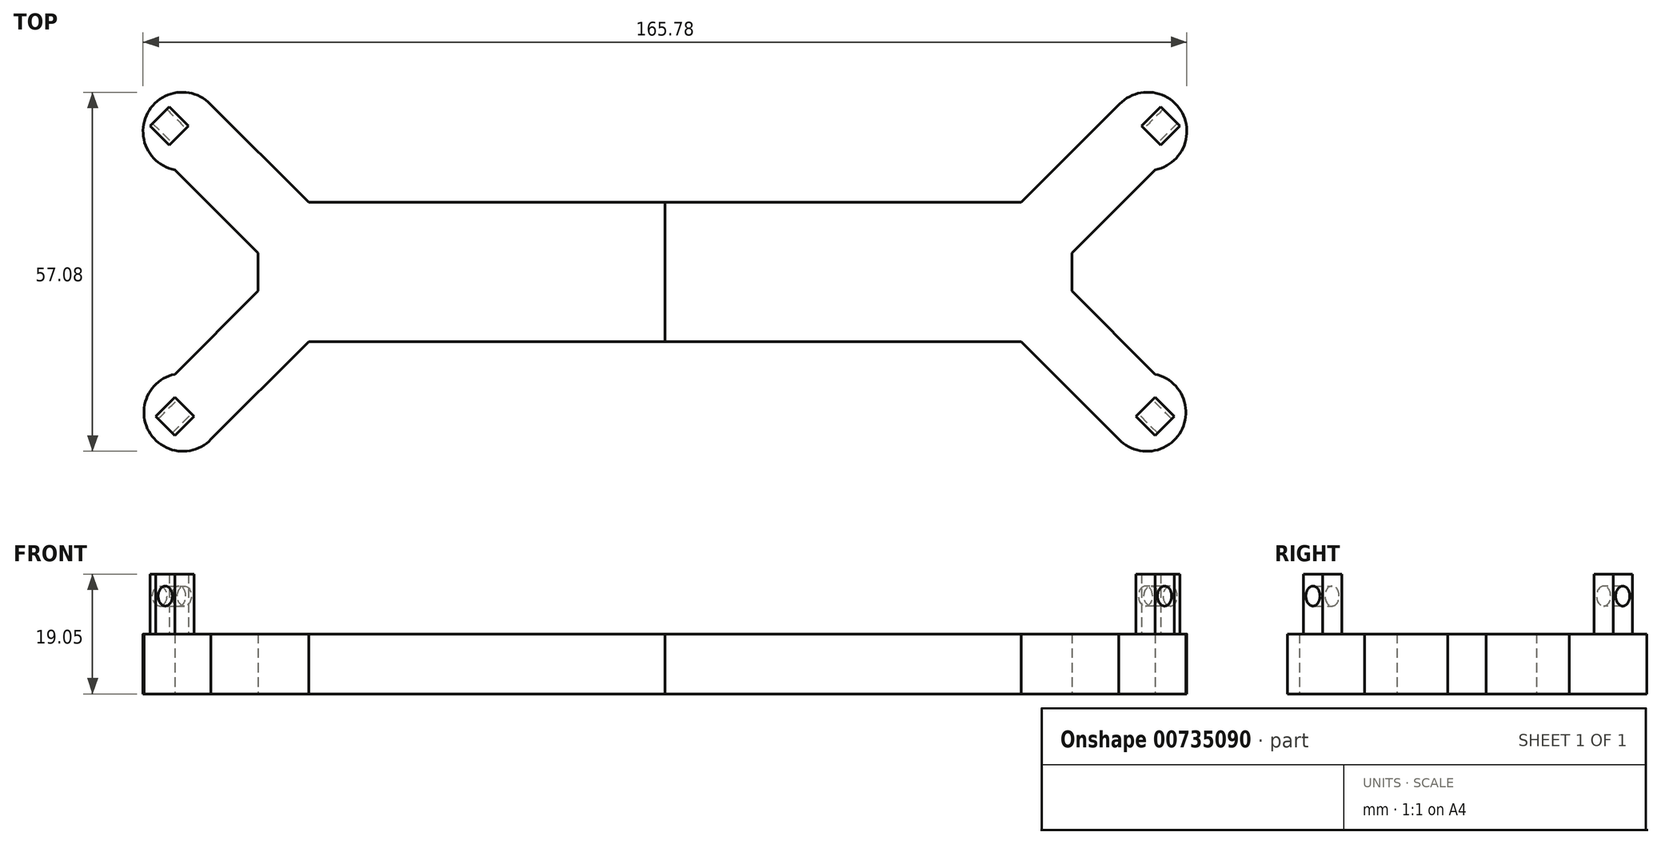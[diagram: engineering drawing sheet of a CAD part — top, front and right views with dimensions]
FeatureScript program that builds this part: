
annotation { "Feature Type Name" : "Feature", "Feature Type Description" : "" }
export const myFeature = defineFeature(function(context is Context, id is Id, definition is map)
    precondition{}
    {
        {
            var Q0;
            Q0=qCreatedBy(makeId("Top.planeOp"),FACE);
            var sketch = newSketch(context, id + "F0", { "sketchPlane" : qUnion([Q0])});
            skLineSegment(sketch, "E0.bottom", {"start": v(0, -10.57) * mm, "end": v(-64.63, -10.57) * mm});
            skLineSegment(sketch, "E0.top", {"start": v(0, 11.58) * mm, "end": v(-64.63, 11.58) * mm});
            skLineSegment(sketch, "E0.left", {"start": v(0, -10.57) * mm, "end": v(0, 11.58) * mm});
            skLineSegment(sketch, "E0.right", {"start": v(-64.63, -10.57) * mm, "end": v(-64.63, 11.58) * mm});
            skLineSegment(sketch, "E1", {"start": v(-56.58, 11.58) * mm, "end": v(-72.3, 27.31) * mm});
            skLineSegment(sketch, "E2", {"start": v(-64.63, 3.53) * mm, "end": v(-77.85, 16.75) * mm});
            skLineSegment(sketch, "E3", {"start": v(-56.58, -10.57) * mm, "end": v(-72.1, -26.09) * mm});
            skLineSegment(sketch, "E4", {"start": v(-64.63, -2.52) * mm, "end": v(-77.85, -15.74) * mm});
            skCircle(sketch, "E5", {"center": v(-76.67, 22.87) * mm, "radius": 6.23 * mm});
            skPoint(sketch, "E5.third.point", {"position": v(-81.03, 27.31) * mm});
            skCircle(sketch, "E6", {"center": v(-76.56, -21.8) * mm, "radius": 6.2 * mm});
            skPoint(sketch, "E6.third.point", {"position": v(-81.03, -26.09) * mm});
            skSolve(sketch);
        }
        {
            var Q0;
            Q0 = qSketchRegion(id + "F0", true);
            extrude(context, id + "F1", {"entities" : qUnion([Q0]), "depth" : 9.52 * mm, "offsetDistance" : 25.4 * mm});
        }
        {
            var Q0;
            Q0=makeQuery(id+"F1.opExtrude","CAP_FACE",FACE,{"disambiguationData":[OSD([sQuery(id+"F0.wireOp",EDGE,"E0.bottom"),sQuery(id+"F0.wireOp",EDGE,"E0.top"),sQuery(id+"F0.wireOp",EDGE,"E0.left"),sQuery(id+"F0.wireOp",EDGE,"E0.right"),sQuery(id+"F0.wireOp",EDGE,"E1"),sQuery(id+"F0.wireOp",EDGE,"E2"),sQuery(id+"F0.wireOp",EDGE,"E3"),sQuery(id+"F0.wireOp",EDGE,"E4"),sQuery(id+"F0.wireOp",EDGE,"E5"),sQuery(id+"F0.wireOp",EDGE,"E6")])],"isStart":false});
            var sketch = newSketch(context, id + "F2", { "sketchPlane" : qUnion([Q0])});
            skLineSegment(sketch, "E7.bottom", {"start": v(-78.74, 20.7) * mm, "end": v(-81.77, 23.74) * mm});
            skLineSegment(sketch, "E7.top", {"start": v(-75.7, 23.74) * mm, "end": v(-78.74, 26.78) * mm});
            skLineSegment(sketch, "E7.left", {"start": v(-78.74, 20.7) * mm, "end": v(-75.7, 23.74) * mm});
            skLineSegment(sketch, "E7.right", {"start": v(-81.77, 23.74) * mm, "end": v(-78.74, 26.78) * mm});
            skPoint(sketch, "E7.middle", {"position": v(-77.85, 23.22) * mm});
            skLineSegment(sketch, "E8.bottom", {"start": v(-74.81, -22.43) * mm, "end": v(-77.85, -19.4) * mm});
            skLineSegment(sketch, "E8.top", {"start": v(-77.85, -25.46) * mm, "end": v(-80.88, -22.43) * mm});
            skLineSegment(sketch, "E8.left", {"start": v(-74.81, -22.43) * mm, "end": v(-77.85, -25.46) * mm});
            skLineSegment(sketch, "E8.right", {"start": v(-77.85, -19.4) * mm, "end": v(-80.88, -22.43) * mm});
            skPoint(sketch, "E8.middle", {"position": v(-77.85, -21.54) * mm});
            skSolve(sketch);
        }
        {
            var Q0;
            Q0 = qSketchRegion(id + "F2", true);
            extrude(context, id + "F3", {"entities" : qUnion([Q0]), "operationType" : NewBodyOperationType.ADD, "depth" : 9.52 * mm, "offsetDistance" : 25.4 * mm});
        }
        {
            var Q0;
            Q0=makeQuery(id+"F3.opExtrude","SWEPT_FACE",FACE,{"disambiguationData":[OSD([sQuery(id+"F2.wireOp",EDGE,"E7.left")])]});
            var sketch = newSketch(context, id + "F4", { "sketchPlane" : qUnion([Q0])});
            skPoint(sketch, "E9", {"position": v(-38.89, 15.54) * mm});
            skPoint(sketch, "E9.positionSnap0", {"position": v(-38.89, 19.05) * mm});
            skSolve(sketch);
        }
        {
            var Q0;
            Q0=makeQuery(id+"F3.opExtrude","SWEPT_FACE",FACE,{"disambiguationData":[OSD([sQuery(id+"F2.wireOp",EDGE,"E8.bottom")])]});
            var sketch = newSketch(context, id + "F5", { "sketchPlane" : qUnion([Q0])});
            skPoint(sketch, "E10", {"position": v(39.19, 15.54) * mm});
            skPoint(sketch, "E10.positionSnap0", {"position": v(39.19, 19.05) * mm});
            skSolve(sketch);
        }
        {
            var Q0;
            Q0=sQuery(id+"F5.wireOp",VERTEX,"E10");
            var Q1;
            Q1=makeQuery(id+"F1.opExtrude","SWEPT_BODY",BODY,{"disambiguationData":[OSD([sQuery(id+"F0.wireOp",EDGE,"E0.bottom"),sQuery(id+"F0.wireOp",EDGE,"E0.top"),sQuery(id+"F0.wireOp",EDGE,"E0.left"),sQuery(id+"F0.wireOp",EDGE,"E0.right"),sQuery(id+"F0.wireOp",EDGE,"E1"),sQuery(id+"F0.wireOp",EDGE,"E2"),sQuery(id+"F0.wireOp",EDGE,"E3"),sQuery(id+"F0.wireOp",EDGE,"E4"),sQuery(id+"F0.wireOp",EDGE,"E5"),sQuery(id+"F0.wireOp",EDGE,"E6")])]});
            hole(context, id + "F6", {"style" : HoleStyle.SIMPLE, "endStyle" : HoleEndStyle.THROUGH, "holeDiameter" : 3.17 * mm, "majorDiameter" : 6.35 * mm, "isTappedThrough" : true, "tappedDepth" : 12.7 * mm, "tapClearance" : 3, "locations" : qUnion([Q0]), "scope" : qUnion([Q1])});
        }
        {
            var Q0;
            Q0=sQuery(id+"F4.wireOp",VERTEX,"E9");
            var Q1;
            Q1=makeQuery(id+"F1.opExtrude","SWEPT_BODY",BODY,{"disambiguationData":[OSD([sQuery(id+"F0.wireOp",EDGE,"E0.bottom"),sQuery(id+"F0.wireOp",EDGE,"E0.top"),sQuery(id+"F0.wireOp",EDGE,"E0.left"),sQuery(id+"F0.wireOp",EDGE,"E0.right"),sQuery(id+"F0.wireOp",EDGE,"E1"),sQuery(id+"F0.wireOp",EDGE,"E2"),sQuery(id+"F0.wireOp",EDGE,"E3"),sQuery(id+"F0.wireOp",EDGE,"E4"),sQuery(id+"F0.wireOp",EDGE,"E5"),sQuery(id+"F0.wireOp",EDGE,"E6")])]});
            hole(context, id + "F7", {"style" : HoleStyle.SIMPLE, "endStyle" : HoleEndStyle.THROUGH, "holeDiameter" : 3.17 * mm, "majorDiameter" : 6.35 * mm, "isTappedThrough" : true, "tappedDepth" : 12.7 * mm, "tapClearance" : 3, "locations" : qUnion([Q0]), "scope" : qUnion([Q1])});
        }
        {
            var Q0;
            Q0=makeQuery(id+"F1.opExtrude","SWEPT_BODY",BODY,{"disambiguationData":[OSD([sQuery(id+"F0.wireOp",EDGE,"E0.bottom"),sQuery(id+"F0.wireOp",EDGE,"E0.top"),sQuery(id+"F0.wireOp",EDGE,"E0.left"),sQuery(id+"F0.wireOp",EDGE,"E0.right"),sQuery(id+"F0.wireOp",EDGE,"E1"),sQuery(id+"F0.wireOp",EDGE,"E2"),sQuery(id+"F0.wireOp",EDGE,"E3"),sQuery(id+"F0.wireOp",EDGE,"E4"),sQuery(id+"F0.wireOp",EDGE,"E5"),sQuery(id+"F0.wireOp",EDGE,"E6")])]});
            var Q1;
            Q1=makeQuery(id+"F1.opExtrude","SWEPT_FACE",FACE,{"disambiguationData":[OSD([sQuery(id+"F0.wireOp",EDGE,"E0.left")])]});
            mirror(context, id + "F8", {"entities" : qUnion([Q0]), "mirrorPlane" : qUnion([Q1])});
        }
    });
